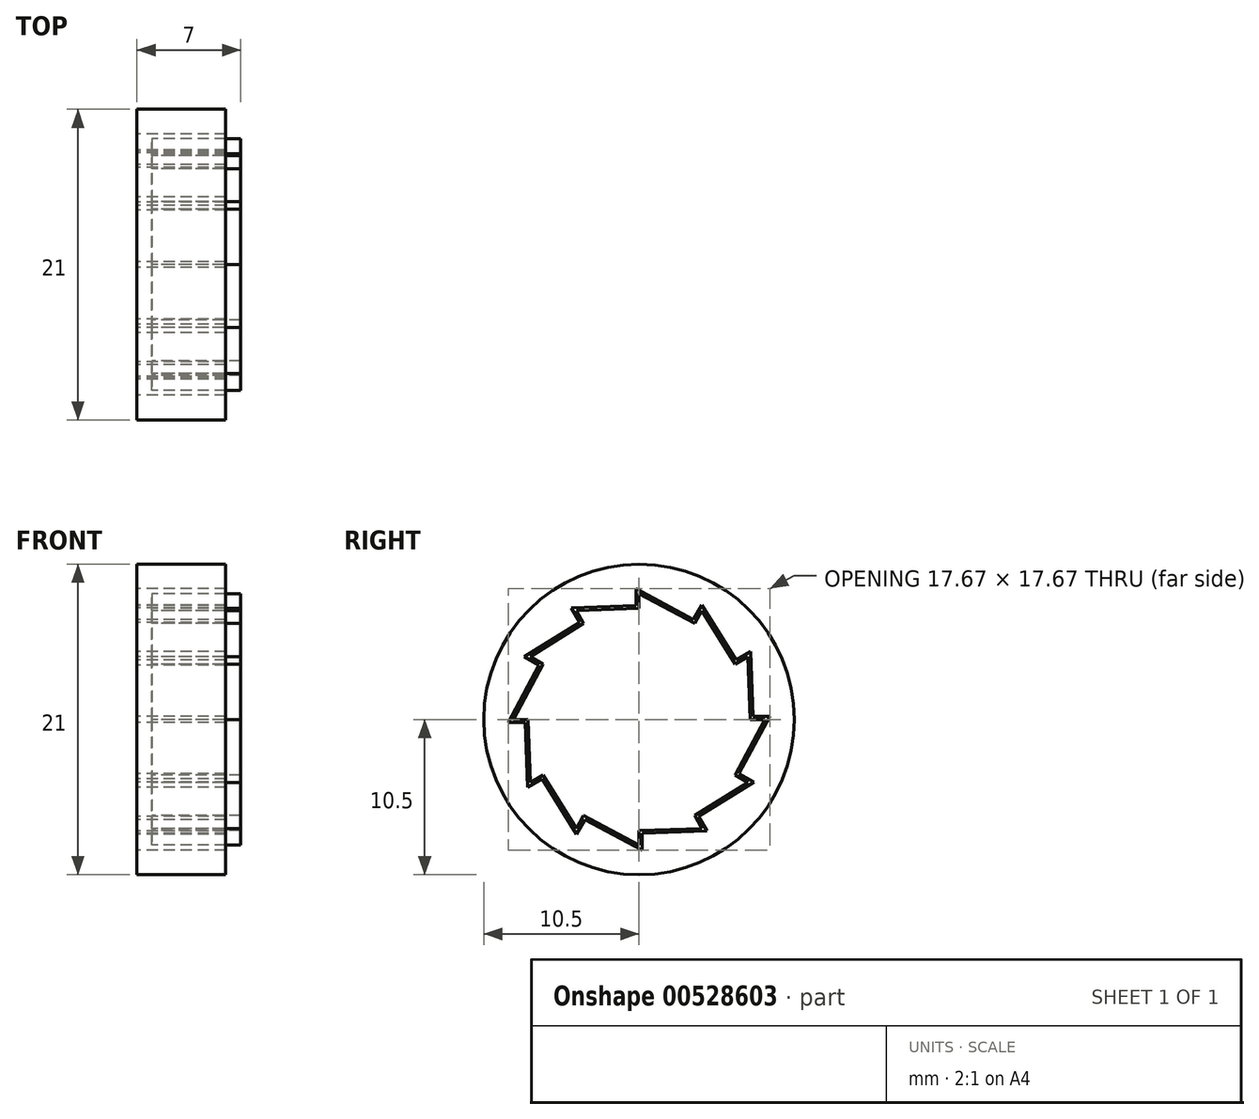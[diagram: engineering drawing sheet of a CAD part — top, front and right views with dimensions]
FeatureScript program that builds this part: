
annotation { "Feature Type Name" : "Feature", "Feature Type Description" : "" }
export const myFeature = defineFeature(function(context is Context, id is Id, definition is map)
    precondition{}
    {
        {
            var Q0;
            Q0=qCreatedBy(makeId("Right.planeOp"),FACE);
            var sketch = newSketch(context, id + "F0", { "sketchPlane" : qUnion([Q0])});
            skCircle(sketch, "E0", {"center": v(0, 0) * mm, "radius": 7.5 * mm});
            skLineSegment(sketch, "E1", {"start": v(0, 7.5) * mm, "end": v(0, 8.5) * mm});
            skLineSegment(sketch, "E2", {"start": v(0, 8.5) * mm, "end": v(3.75, 6.5) * mm});
            skLineSegment(sketch, "E3.1.0", {"start": v(4.25, 7.36) * mm, "end": v(6.5, 3.75) * mm});
            skLineSegment(sketch, "E3.1.1", {"start": v(3.75, 6.5) * mm, "end": v(4.25, 7.36) * mm});
            skLineSegment(sketch, "E3.2.0", {"start": v(7.36, 4.25) * mm, "end": v(7.5, 0) * mm});
            skLineSegment(sketch, "E3.2.1", {"start": v(6.5, 3.75) * mm, "end": v(7.36, 4.25) * mm});
            skLineSegment(sketch, "E3.3.0", {"start": v(8.5, 0) * mm, "end": v(6.5, -3.75) * mm});
            skLineSegment(sketch, "E3.3.1", {"start": v(7.5, 0) * mm, "end": v(8.5, 0) * mm});
            skLineSegment(sketch, "E3.4.0", {"start": v(7.36, -4.25) * mm, "end": v(3.75, -6.5) * mm});
            skLineSegment(sketch, "E3.4.1", {"start": v(6.5, -3.75) * mm, "end": v(7.36, -4.25) * mm});
            skLineSegment(sketch, "E3.5.0", {"start": v(4.25, -7.36) * mm, "end": v(0, -7.5) * mm});
            skLineSegment(sketch, "E3.5.1", {"start": v(3.75, -6.5) * mm, "end": v(4.25, -7.36) * mm});
            skLineSegment(sketch, "E3.6.0", {"start": v(0, -8.5) * mm, "end": v(-3.75, -6.5) * mm});
            skLineSegment(sketch, "E3.6.1", {"start": v(0, -7.5) * mm, "end": v(0, -8.5) * mm});
            skLineSegment(sketch, "E3.7.0", {"start": v(-4.25, -7.36) * mm, "end": v(-6.5, -3.75) * mm});
            skLineSegment(sketch, "E3.7.1", {"start": v(-3.75, -6.5) * mm, "end": v(-4.25, -7.36) * mm});
            skLineSegment(sketch, "E3.8.0", {"start": v(-7.36, -4.25) * mm, "end": v(-7.5, 0) * mm});
            skLineSegment(sketch, "E3.8.1", {"start": v(-6.5, -3.75) * mm, "end": v(-7.36, -4.25) * mm});
            skLineSegment(sketch, "E3.9.0", {"start": v(-8.5, 0) * mm, "end": v(-6.5, 3.75) * mm});
            skLineSegment(sketch, "E3.9.1", {"start": v(-7.5, 0) * mm, "end": v(-8.5, 0) * mm});
            skLineSegment(sketch, "E3.10.0", {"start": v(-7.36, 4.25) * mm, "end": v(-3.75, 6.5) * mm});
            skLineSegment(sketch, "E3.10.1", {"start": v(-6.5, 3.75) * mm, "end": v(-7.36, 4.25) * mm});
            skLineSegment(sketch, "E3.11.0", {"start": v(-4.25, 7.36) * mm, "end": v(0, 7.5) * mm});
            skLineSegment(sketch, "E3.11.1", {"start": v(-3.75, 6.5) * mm, "end": v(-4.25, 7.36) * mm});
            skLineSegment(sketch, "E3.anchor1", {"start": v(0, 0) * mm, "end": v(0, 8.5) * mm, "construction": true});
            skLineSegment(sketch, "E3.anchor2", {"start": v(0, 0) * mm, "end": v(-4.25, 7.36) * mm, "construction": true});
            skLineSegment(sketch, "E4.0", {"start": v(-4.24, -7.75) * mm, "end": v(-6.56, -4.02) * mm});
            skLineSegment(sketch, "E4.1", {"start": v(3.67, 6.76) * mm, "end": v(4.24, 7.75) * mm});
            skLineSegment(sketch, "E4.2", {"start": v(-0.2, 8.83) * mm, "end": v(3.67, 6.76) * mm});
            skLineSegment(sketch, "E4.3", {"start": v(-0.2, 7.7) * mm, "end": v(-0.2, 8.83) * mm});
            skLineSegment(sketch, "E4.4", {"start": v(-4.6, 7.55) * mm, "end": v(-0.2, 7.7) * mm});
            skLineSegment(sketch, "E4.5", {"start": v(-4.02, 6.56) * mm, "end": v(-4.6, 7.55) * mm});
            skLineSegment(sketch, "E4.6", {"start": v(-7.75, 4.24) * mm, "end": v(-4.02, 6.56) * mm});
            skLineSegment(sketch, "E4.7", {"start": v(-7.55, -4.6) * mm, "end": v(-7.7, -0.2) * mm});
            skLineSegment(sketch, "E4.8", {"start": v(-7.7, -0.2) * mm, "end": v(-8.83, -0.2) * mm});
            skLineSegment(sketch, "E4.9", {"start": v(-8.83, -0.2) * mm, "end": v(-6.76, 3.67) * mm});
            skLineSegment(sketch, "E4.10", {"start": v(-6.76, 3.67) * mm, "end": v(-7.75, 4.24) * mm});
            skLineSegment(sketch, "E4.11", {"start": v(4.24, 7.75) * mm, "end": v(6.56, 4.02) * mm});
            skLineSegment(sketch, "E4.12", {"start": v(-6.56, -4.02) * mm, "end": v(-7.55, -4.6) * mm});
            skLineSegment(sketch, "E4.13", {"start": v(6.56, 4.02) * mm, "end": v(7.55, 4.6) * mm});
            skLineSegment(sketch, "E4.14", {"start": v(7.55, 4.6) * mm, "end": v(7.7, 0.2) * mm});
            skLineSegment(sketch, "E4.15", {"start": v(7.7, 0.2) * mm, "end": v(8.83, 0.2) * mm});
            skLineSegment(sketch, "E4.16", {"start": v(8.83, 0.2) * mm, "end": v(6.76, -3.67) * mm});
            skLineSegment(sketch, "E4.17", {"start": v(6.76, -3.67) * mm, "end": v(7.75, -4.24) * mm});
            skLineSegment(sketch, "E4.18", {"start": v(7.75, -4.24) * mm, "end": v(4.02, -6.56) * mm});
            skLineSegment(sketch, "E4.19", {"start": v(4.02, -6.56) * mm, "end": v(4.6, -7.55) * mm});
            skLineSegment(sketch, "E4.20", {"start": v(4.6, -7.55) * mm, "end": v(0.2, -7.7) * mm});
            skLineSegment(sketch, "E4.21", {"start": v(0.2, -7.7) * mm, "end": v(0.2, -8.83) * mm});
            skLineSegment(sketch, "E4.22", {"start": v(0.2, -8.83) * mm, "end": v(-3.67, -6.76) * mm});
            skLineSegment(sketch, "E4.23", {"start": v(-3.67, -6.76) * mm, "end": v(-4.24, -7.75) * mm});
            skCircle(sketch, "E5.0", {"center": v(0, 0) * mm, "radius": 10.5 * mm});
            skSolve(sketch);
        }
        {
            var Q0;
            {var subQ0=sQuery(id+"F0.wireOp",EDGE,"E3.10.1");Q0=makeQuery(id+"F0.imprint","IMPRINT",FACE,{"disambiguationData":[TD([[makeQuery(id+"F0.imprint","IMPRINT",EDGE,{"derivedFrom":subQ0}),-1.0]])]});}
            var Q1;
            {var subQ1=sQuery(id+"F0.wireOp",EDGE,"E0");var subQ14=sQuery(id+"F0.wireOp",EDGE,"E3.2.0");var subQ16=makeQuery(id+"F0.imprint","INTERSECT",VERTEX,{"derivedFrom":[subQ1,subQ14]});Q1=makeQuery(id+"F0.imprint","IMPRINT",FACE,{"disambiguationData":[TD([[makeQuery(id+"F0.imprint","IMPRINT",EDGE,{"disambiguationData":[TD([[subQ16,-1.0]])],"derivedFrom":subQ1}),1.0]])]});}
            var Q2;
            {var subQ0=sQuery(id+"F0.wireOp",EDGE,"E3.11.1");Q2=makeQuery(id+"F0.imprint","IMPRINT",FACE,{"disambiguationData":[TD([[makeQuery(id+"F0.imprint","IMPRINT",EDGE,{"derivedFrom":subQ0}),-1.0]])]});}
            var Q3;
            {var subQ0=sQuery(id+"F0.wireOp",EDGE,"E1");Q3=makeQuery(id+"F0.imprint","IMPRINT",FACE,{"disambiguationData":[TD([[makeQuery(id+"F0.imprint","IMPRINT",EDGE,{"derivedFrom":subQ0}),-1.0]])]});}
            var Q4;
            {var subQ0=sQuery(id+"F0.wireOp",EDGE,"E3.1.1");Q4=makeQuery(id+"F0.imprint","IMPRINT",FACE,{"disambiguationData":[TD([[makeQuery(id+"F0.imprint","IMPRINT",EDGE,{"derivedFrom":subQ0}),-1.0]])]});}
            var Q5;
            {var subQ0=sQuery(id+"F0.wireOp",EDGE,"E3.2.1");Q5=makeQuery(id+"F0.imprint","IMPRINT",FACE,{"disambiguationData":[TD([[makeQuery(id+"F0.imprint","IMPRINT",EDGE,{"derivedFrom":subQ0}),-1.0]])]});}
            var Q6;
            {var subQ0=sQuery(id+"F0.wireOp",EDGE,"E3.3.1");Q6=makeQuery(id+"F0.imprint","IMPRINT",FACE,{"disambiguationData":[TD([[makeQuery(id+"F0.imprint","IMPRINT",EDGE,{"derivedFrom":subQ0}),-1.0]])]});}
            var Q7;
            {var subQ0=sQuery(id+"F0.wireOp",EDGE,"E3.4.1");Q7=makeQuery(id+"F0.imprint","IMPRINT",FACE,{"disambiguationData":[TD([[makeQuery(id+"F0.imprint","IMPRINT",EDGE,{"derivedFrom":subQ0}),-1.0]])]});}
            var Q8;
            {var subQ0=sQuery(id+"F0.wireOp",EDGE,"E3.5.1");Q8=makeQuery(id+"F0.imprint","IMPRINT",FACE,{"disambiguationData":[TD([[makeQuery(id+"F0.imprint","IMPRINT",EDGE,{"derivedFrom":subQ0}),-1.0]])]});}
            var Q9;
            {var subQ0=sQuery(id+"F0.wireOp",EDGE,"E3.6.1");Q9=makeQuery(id+"F0.imprint","IMPRINT",FACE,{"disambiguationData":[TD([[makeQuery(id+"F0.imprint","IMPRINT",EDGE,{"derivedFrom":subQ0}),-1.0]])]});}
            var Q10;
            {var subQ0=sQuery(id+"F0.wireOp",EDGE,"E3.7.1");Q10=makeQuery(id+"F0.imprint","IMPRINT",FACE,{"disambiguationData":[TD([[makeQuery(id+"F0.imprint","IMPRINT",EDGE,{"derivedFrom":subQ0}),-1.0]])]});}
            var Q11;
            {var subQ0=sQuery(id+"F0.wireOp",EDGE,"E3.8.1");Q11=makeQuery(id+"F0.imprint","IMPRINT",FACE,{"disambiguationData":[TD([[makeQuery(id+"F0.imprint","IMPRINT",EDGE,{"derivedFrom":subQ0}),-1.0]])]});}
            var Q12;
            {var subQ0=sQuery(id+"F0.wireOp",EDGE,"E3.9.1");Q12=makeQuery(id+"F0.imprint","IMPRINT",FACE,{"disambiguationData":[TD([[makeQuery(id+"F0.imprint","IMPRINT",EDGE,{"derivedFrom":subQ0}),-1.0]])]});}
            extrude(context, id + "F1", {"entities" : qUnion([Q0, Q1, Q2, Q3, Q4, Q5, Q6, Q7, Q8, Q9, Q10, Q11, Q12]), "depth" : 6 * mm, "offsetDistance" : 25 * mm});
        }
        {
            var Q0;
            Q0=makeQuery(id+"F0.imprint","IMPRINT",FACE,{"disambiguationData":[TD([[makeQuery(id+"F0.imprint","IMPRINT",EDGE,{"derivedFrom":sQuery(id+"F0.wireOp",EDGE,"E4.0")}),1.0]])]});
            extrude(context, id + "F2", {"entities" : qUnion([Q0]), "depth" : 5 * mm, "offsetDistance" : 25 * mm, "hasSecondDirection" : true, "secondDirectionOppositeDirection" : true, "secondDirectionDepth" : 1 * mm});
        }
    });
